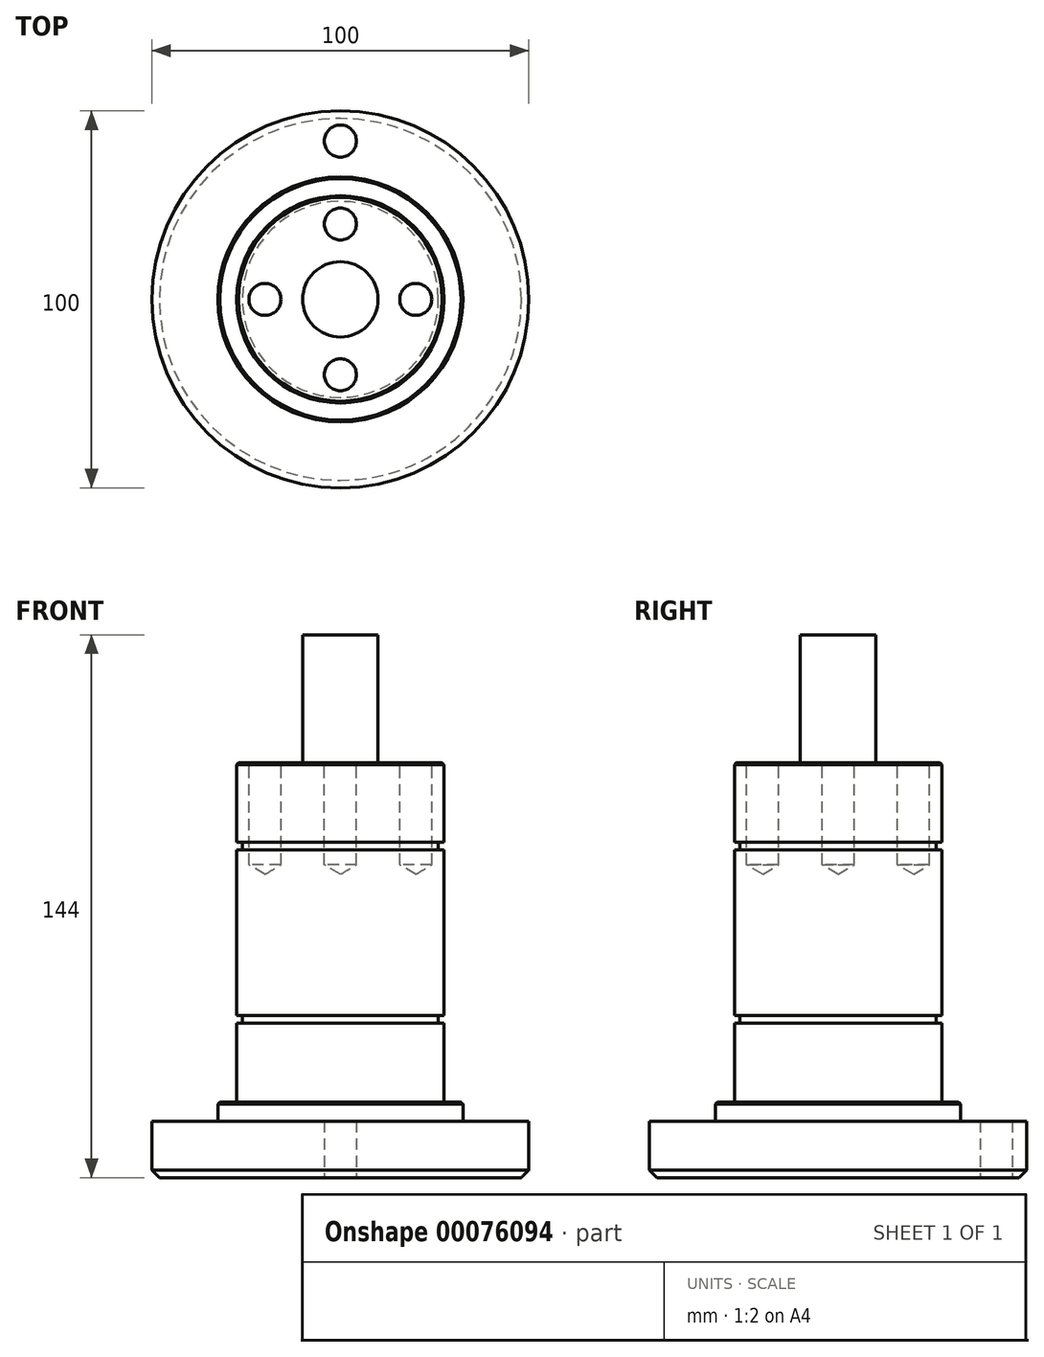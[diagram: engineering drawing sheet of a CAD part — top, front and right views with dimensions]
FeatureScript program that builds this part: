
annotation { "Feature Type Name" : "Feature", "Feature Type Description" : "" }
export const myFeature = defineFeature(function(context is Context, id is Id, definition is map)
    precondition{}
    {
        {
            var Q0;
            Q0=qCreatedBy(makeId("Top.planeOp"),FACE);
            var sketch = newSketch(context, id + "F0", { "sketchPlane" : qUnion([Q0])});
            skCircle(sketch, "E0", {"center": v(0, 0) * mm, "radius": 50 * mm});
            skSolve(sketch);
        }
        {
            var Q0;
            Q0 = qSketchRegion(id + "F0", true);
            extrude(context, id + "F1", {"entities" : qUnion([Q0]), "depth" : 15 * mm});
        }
        {
            var Q0;
            Q0=makeQuery(id+"F1.opExtrude","CAP_FACE",FACE,{"disambiguationData":[OSD([sQuery(id+"F0.wireOp",EDGE,"E0")])],"isStart":false});
            var sketch = newSketch(context, id + "F2", { "sketchPlane" : qUnion([Q0])});
            skCircle(sketch, "E1", {"center": v(0, 0) * mm, "radius": 32.5 * mm});
            skSolve(sketch);
        }
        {
            var Q0;
            Q0 = qSketchRegion(id + "F2", true);
            extrude(context, id + "F3", {"entities" : qUnion([Q0]), "operationType" : NewBodyOperationType.ADD, "depth" : 5 * mm});
        }
        {
            var Q0;
            Q0=makeQuery(id+"F3.opExtrude","CAP_FACE",FACE,{"disambiguationData":[OSD([sQuery(id+"F2.wireOp",EDGE,"E1")])],"isStart":false});
            var sketch = newSketch(context, id + "F4", { "sketchPlane" : qUnion([Q0])});
            skCircle(sketch, "E2", {"center": v(0, 0) * mm, "radius": 27.5 * mm});
            skSolve(sketch);
        }
        {
            var Q0;
            Q0 = qSketchRegion(id + "F4", true);
            extrude(context, id + "F5", {"entities" : qUnion([Q0]), "operationType" : NewBodyOperationType.ADD, "depth" : 21 * mm});
        }
        {
            var Q0;
            Q0=makeQuery(id+"F5.opExtrude","CAP_FACE",FACE,{"disambiguationData":[OSD([sQuery(id+"F4.wireOp",EDGE,"E2")])],"isStart":false});
            var sketch = newSketch(context, id + "F6", { "sketchPlane" : qUnion([Q0])});
            skCircle(sketch, "E3", {"center": v(0, 0) * mm, "radius": 26 * mm});
            skSolve(sketch);
        }
        {
            var Q0;
            Q0 = qSketchRegion(id + "F6", true);
            extrude(context, id + "F7", {"entities" : qUnion([Q0]), "operationType" : NewBodyOperationType.ADD, "depth" : 2 * mm});
        }
        {
            var Q0;
            Q0=makeQuery(id+"F7.opExtrude","CAP_FACE",FACE,{"disambiguationData":[OSD([sQuery(id+"F6.wireOp",EDGE,"E3")])],"isStart":false});
            var sketch = newSketch(context, id + "F8", { "sketchPlane" : qUnion([Q0])});
            skCircle(sketch, "E4", {"center": v(0, 0) * mm, "radius": 27.5 * mm});
            skSolve(sketch);
        }
        {
            var Q0;
            Q0 = qSketchRegion(id + "F8", true);
            extrude(context, id + "F9", {"entities" : qUnion([Q0]), "operationType" : NewBodyOperationType.ADD, "depth" : 44 * mm});
        }
        {
            var Q0;
            Q0=makeQuery(id+"F9.opExtrude","CAP_FACE",FACE,{"disambiguationData":[OSD([sQuery(id+"F8.wireOp",EDGE,"E4")])],"isStart":false});
            var sketch = newSketch(context, id + "F10", { "sketchPlane" : qUnion([Q0])});
            skCircle(sketch, "E5", {"center": v(0, 0) * mm, "radius": 26 * mm});
            skSolve(sketch);
        }
        {
            var Q0;
            Q0 = qSketchRegion(id + "F10", true);
            extrude(context, id + "F11", {"entities" : qUnion([Q0]), "operationType" : NewBodyOperationType.ADD, "depth" : 2 * mm});
        }
        {
            var Q0;
            Q0=makeQuery(id+"F11.opExtrude","CAP_FACE",FACE,{"disambiguationData":[OSD([sQuery(id+"F10.wireOp",EDGE,"E5")])],"isStart":false});
            var sketch = newSketch(context, id + "F12", { "sketchPlane" : qUnion([Q0])});
            skCircle(sketch, "E6", {"center": v(0, 0) * mm, "radius": 27.5 * mm});
            skSolve(sketch);
        }
        {
            var Q0;
            Q0 = qSketchRegion(id + "F12", true);
            extrude(context, id + "F13", {"entities" : qUnion([Q0]), "operationType" : NewBodyOperationType.ADD, "depth" : 21 * mm});
        }
        {
            var Q0;
            Q0=makeQuery(id+"F13.opExtrude","CAP_FACE",FACE,{"disambiguationData":[OSD([sQuery(id+"F12.wireOp",EDGE,"E6")])],"isStart":false});
            var sketch = newSketch(context, id + "F14", { "sketchPlane" : qUnion([Q0])});
            skCircle(sketch, "E7", {"center": v(0, 0) * mm, "radius": 10 * mm});
            skSolve(sketch);
        }
        {
            var Q0;
            Q0 = qSketchRegion(id + "F14", true);
            extrude(context, id + "F15", {"entities" : qUnion([Q0]), "operationType" : NewBodyOperationType.ADD, "depth" : 34 * mm});
        }
        {
            var Q0;
            Q0=makeQuery(id+"F1.opExtrude","CAP_FACE",FACE,{"disambiguationData":[OSD([sQuery(id+"F0.wireOp",EDGE,"E0")])],"isStart":true});
            var sketch = newSketch(context, id + "F16", { "sketchPlane" : qUnion([Q0])});
            skLineSegment(sketch, "E8", {"start": v(0, 0) * mm, "end": v(0, 42) * mm});
            skLineSegment(sketch, "E9", {"start": v(0, 0) * mm, "end": v(-42, 0) * mm});
            skLineSegment(sketch, "E10.MirrorCS", {"start": v(0, 0) * mm, "end": v(42, 0) * mm});
            skLineSegment(sketch, "E11.MirrorCS", {"start": v(0, 0) * mm, "end": v(0, -42) * mm});
            skSolve(sketch);
        }
        {
            var Q0;
            Q0=sQuery(id+"F16.wireOp",VERTEX,"E8.end");
            var Q1;
            Q1=sQuery(id+"F16.wireOp",VERTEX,"E10.MirrorCS.end");
            var Q2;
            Q2=sQuery(id+"F16.wireOp",VERTEX,"E11.MirrorCS.end");
            var Q3;
            Q3=sQuery(id+"F16.wireOp",VERTEX,"E9.end");
            var Q4;
            Q4=makeQuery(id+"F1.opExtrude","SWEPT_BODY",BODY,{"disambiguationData":[OSD([sQuery(id+"F0.wireOp",EDGE,"E0")])]});
            hole(context, id + "F17", {"style" : HoleStyle.SIMPLE, "endStyle" : HoleEndStyle.THROUGH, "holeDiameter" : 8.5 * mm, "startFromSketch" : true, "locations" : qUnion([Q0, Q1, Q2, Q3]), "scope" : qUnion([Q4]), "isTappedThrough" : true});
        }
        {
            var Q0;
            Q0=makeQuery(id+"F13.opExtrude","CAP_FACE",FACE,{"disambiguationData":[OSD([sQuery(id+"F12.wireOp",EDGE,"E6")])],"isStart":false});
            var sketch = newSketch(context, id + "F18", { "sketchPlane" : qUnion([Q0])});
            skLineSegment(sketch, "E12", {"start": v(0, 0) * mm, "end": v(20, 0) * mm});
            skLineSegment(sketch, "E13", {"start": v(0, 0) * mm, "end": v(-20, 0) * mm});
            skLineSegment(sketch, "E14", {"start": v(0, 0) * mm, "end": v(0, -20) * mm});
            skLineSegment(sketch, "E15", {"start": v(0, 0) * mm, "end": v(0, 20) * mm});
            skSolve(sketch);
        }
        {
            var Q0;
            Q0=sQuery(id+"F18.wireOp",VERTEX,"E15.end");
            var Q1;
            Q1=sQuery(id+"F18.wireOp",VERTEX,"E12.end");
            var Q2;
            Q2=sQuery(id+"F18.wireOp",VERTEX,"E14.end");
            var Q3;
            Q3=sQuery(id+"F18.wireOp",VERTEX,"E13.end");
            var Q4;
            Q4=makeQuery(id+"F1.opExtrude","SWEPT_BODY",BODY,{"disambiguationData":[OSD([sQuery(id+"F0.wireOp",EDGE,"E0")])]});
            hole(context, id + "F19", {"style" : HoleStyle.SIMPLE, "endStyle" : HoleEndStyle.BLIND, "holeDiameter" : 8.5 * mm, "holeDepth" : 27 * mm, "startFromSketch" : true, "locations" : qUnion([Q0, Q1, Q2, Q3]), "scope" : qUnion([Q4])});
        }
        {
            var Q0;
            Q0=makeQuery(id+"F1.opExtrude","CAP_EDGE",EDGE,{"disambiguationData":[OSD([sQuery(id+"F0.wireOp",EDGE,"E0")])],"isStart":true});
            chamfer(context, id + "F20", {"entities" : qUnion([Q0]), "width" : 2 * mm, "tangentPropagation" : true});
        }
        {
            var Q0;
            Q0=makeQuery(id+"F3.opExtrude","CAP_EDGE",EDGE,{"disambiguationData":[OSD([sQuery(id+"F2.wireOp",EDGE,"E1")])],"isStart":false});
            chamfer(context, id + "F21", {"entities" : qUnion([Q0]), "width" : 0.5 * mm, "tangentPropagation" : true});
        }
        {
            var Q0;
            Q0=makeQuery(id+"F13.opExtrude","CAP_EDGE",EDGE,{"disambiguationData":[OSD([sQuery(id+"F12.wireOp",EDGE,"E6")])],"isStart":false});
            chamfer(context, id + "F22", {"entities" : qUnion([Q0]), "width" : 0.5 * mm, "tangentPropagation" : true});
        }
    });
